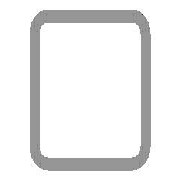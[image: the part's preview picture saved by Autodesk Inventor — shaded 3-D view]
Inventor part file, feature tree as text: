
AUTODESK INVENTOR PART (.ipt)
format: ipt  version: 2025.1 (Build 291241020, 241B)  size: 142,848 bytes
history: native  units: mm (DEFAULTED — no unit token found)
features: other x4, sketch x1, plane x1
ambient origin geometry x8: Origin, YZ Plane, XZ Plane, XY Plane, X Axis, Y Axis, Z Axis, Center Point
bodies: Solid1 (feature_tree), Body (feature_tree)
feature tree (6):
  parser-record x1  (decoder bookkeeping rows leaked as tree rows — omitted from the tree; the rows remain in map.json)
  other  "Driven Length"
  other  "Start plane"
  other  "End plane"
  sketch  "Sketch3"  dims[d3=2750.0mm d4=0.0mm d7=8.0mm d9=100.0mm d11=100.0mm d12=4.0mm d13=-0.0mm d14=2750.0mm d15=50.0mm d16=50.0mm d17=90.0deg d18=2750.0mm]
  plane  "Work Plane3"
